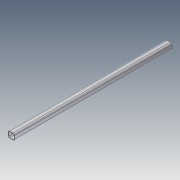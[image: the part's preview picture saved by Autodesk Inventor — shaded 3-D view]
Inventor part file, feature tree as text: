
AUTODESK INVENTOR PART (.ipt)
format: ipt  version: unknown  size: 197,120 bytes
history: native  units: in
note: dims shown in document units (in); Inventor stores cm internally (conversion verified against a paired STEP export)
features: extrude x2, sketch x2
ambient origin geometry x8: Origin, YZ Plane, XZ Plane, XY Plane, X Axis, Y Axis, Z Axis, Center Point
bodies: Solid1 (feature_tree)
feature tree (4):
  extrude  "Extrusion1"  Depth=0.375in
  extrude  "Extrusion2"  Depth=37.125in TaperAngle=0.0deg
  sketch  "Sketch1"  dims[d0=1.5in d1=0.375in]
  sketch  "Sketch2"  dims[d2=0.125in d3=37.125in d4=0.0in d5=0.0206in d6=0.0206in d7=37.0in d8=0.0in]
